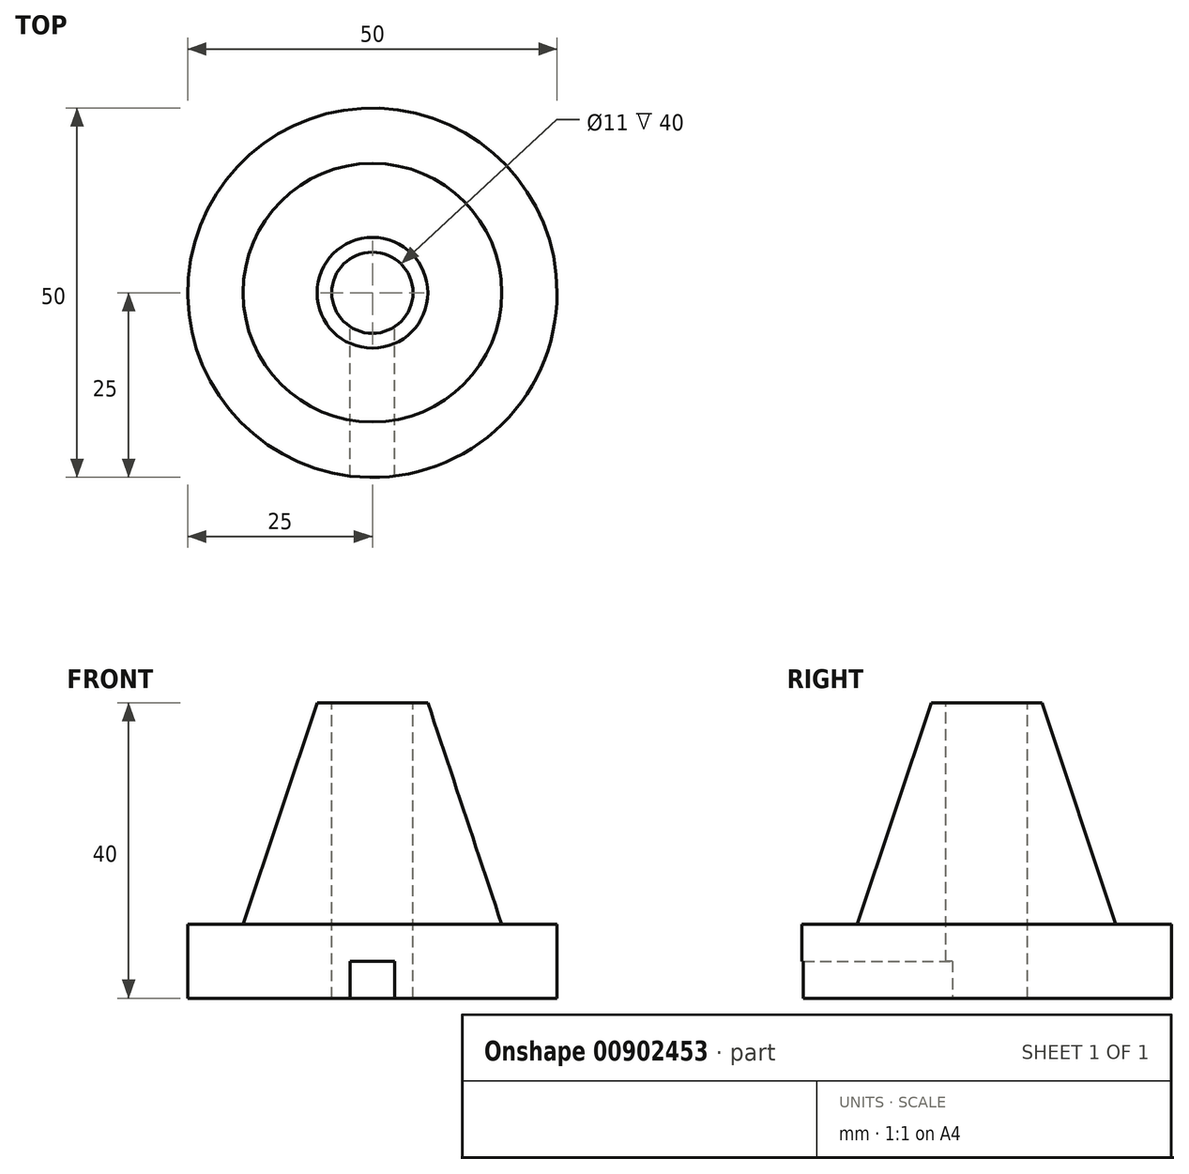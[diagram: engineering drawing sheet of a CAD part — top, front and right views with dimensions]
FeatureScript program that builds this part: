
annotation { "Feature Type Name" : "Feature", "Feature Type Description" : "" }
export const myFeature = defineFeature(function(context is Context, id is Id, definition is map)
    precondition{}
    {
        {
            var Q0;
            Q0=qCreatedBy(makeId("Top.planeOp"),FACE);
            var sketch = newSketch(context, id + "F0", { "sketchPlane" : qUnion([Q0])});
            skArc(sketch, "E0", {"start": v(3, -24.82) * mm, "mid": v(0, 25) * mm, "end": v(-3, -24.82) * mm});
            skLineSegment(sketch, "E1", {"start": v(3, -24.82) * mm, "end": v(3, -4.6) * mm});
            skLineSegment(sketch, "E2", {"start": v(-3, -24.82) * mm, "end": v(-3, -4.6) * mm});
            skLineSegment(sketch, "E3", {"start": v(-3, -4.6) * mm, "end": v(3, -4.6) * mm});
            skSolve(sketch);
        }
        {
            var Q0;
            Q0 = qSketchRegion(id + "F0", true);
            extrude(context, id + "F1", {"entities" : qUnion([Q0]), "depth" : 5 * mm, "offsetDistance" : 25 * mm});
        }
        {
            var Q0;
            Q0=makeQuery(id+"F1.opExtrude","CAP_FACE",FACE,{"disambiguationData":[OSD([sQuery(id+"F0.wireOp",EDGE,"E0"),sQuery(id+"F0.wireOp",EDGE,"onPXodx1-0HZF-bY3a-4zoJ-UEnkSIDCSzZy"),sQuery(id+"F0.wireOp",EDGE,"E1"),sQuery(id+"F0.wireOp",EDGE,"E2")])],"isStart":false});
            var sketch = newSketch(context, id + "F2", { "sketchPlane" : qUnion([Q0])});
            skCircle(sketch, "E4", {"center": v(0, 0) * mm, "radius": 25 * mm});
            skSolve(sketch);
        }
        {
            var Q0;
            Q0 = qSketchRegion(id + "F2", true);
            extrude(context, id + "F3", {"entities" : qUnion([Q0]), "operationType" : NewBodyOperationType.ADD, "depth" : 5 * mm, "offsetDistance" : 25 * mm});
        }
        {
            var Q0;
            Q0=makeQuery(id+"F3.opExtrude","CAP_FACE",FACE,{"disambiguationData":[OSD([sQuery(id+"F2.wireOp",EDGE,"E4")])],"isStart":false});
            var sketch = newSketch(context, id + "F4", { "sketchPlane" : qUnion([Q0])});
            skCircle(sketch, "E5", {"center": v(0, 0) * mm, "radius": 17.5 * mm});
            skSolve(sketch);
        }
        {
            var Q0;
            Q0=makeQuery(id+"F4.imprint","IMPRINT",FACE,{"disambiguationData":[TD([[makeQuery(id+"F4.imprint","IMPRINT",EDGE,{"derivedFrom":sQuery(id+"F4.wireOp",EDGE,"E5")}),-1.0]])]});
            cPlane(context, id + "F5", {"entities" : qUnion([Q0]), "cplaneType" : CPlaneType.OFFSET, "offset" : 30 * mm, "width" : 150 * mm, "height" : 150 * mm});
        }
        {
            var Q0;
            Q0=qCreatedBy(id+"F5.planeOp",FACE);
            var sketch = newSketch(context, id + "F6", { "sketchPlane" : qUnion([Q0])});
            skCircle(sketch, "E6", {"center": v(0, 0) * mm, "radius": 7.5 * mm});
            skSolve(sketch);
        }
        {
            var Q1;
            Q1=makeQuery(id+"F6.imprint","IMPRINT",FACE,{"disambiguationData":[TD([[makeQuery(id+"F6.imprint","IMPRINT",EDGE,{"derivedFrom":sQuery(id+"F6.wireOp",EDGE,"E6")}),1.0]])]});
            var Q2;
            Q2=makeQuery(id+"F4.imprint","IMPRINT",FACE,{"disambiguationData":[TD([[makeQuery(id+"F4.imprint","IMPRINT",EDGE,{"derivedFrom":sQuery(id+"F4.wireOp",EDGE,"E5")}),1.0]])]});
            loft(context, id + "F7", {"operationType" : NewBodyOperationType.ADD, "sheetProfilesArray" : [{ "sheetProfileEntities" : qUnion([Q1]) }, { "sheetProfileEntities" : qUnion([Q2]) }]});
        }
        {
            var Q0;
            Q0=makeQuery(id+"F7.opLoft","CAP_FACE",FACE,{"disambiguationData":[OSD([makeQuery(id+"F6.imprint","IMPRINT",FACE,{"disambiguationData":[TD([[makeQuery(id+"F6.imprint","IMPRINT",EDGE,{"derivedFrom":sQuery(id+"F6.wireOp",EDGE,"E6")}),1.0]])]})])],"isStart":true});
            var sketch = newSketch(context, id + "F8", { "sketchPlane" : qUnion([Q0])});
            skCircle(sketch, "E7", {"center": v(0, 0) * mm, "radius": 5.5 * mm});
            skSolve(sketch);
        }
        {
            var Q0;
            Q0=makeQuery(id+"F8.imprint","IMPRINT",FACE,{"disambiguationData":[TD([[makeQuery(id+"F8.imprint","IMPRINT",EDGE,{"derivedFrom":sQuery(id+"F8.wireOp",EDGE,"E7")}),1.0]])]});
            var Q1;
            Q1=makeQuery(id+"F1.opExtrude","CAP_FACE",FACE,{"disambiguationData":[OSD([sQuery(id+"F0.wireOp",EDGE,"E0"),sQuery(id+"F0.wireOp",EDGE,"E1"),sQuery(id+"F0.wireOp",EDGE,"E2"),sQuery(id+"F0.wireOp",EDGE,"E3")])],"isStart":true});
            extrude(context, id + "F9", {"entities" : qUnion([Q0]), "operationType" : NewBodyOperationType.REMOVE, "endBound" : BoundingType.UP_TO_SURFACE, "oppositeDirection" : true, "depth" : 25 * mm, "endBoundEntityFace" : qUnion([Q1]), "offsetDistance" : 25 * mm});
        }
    });
